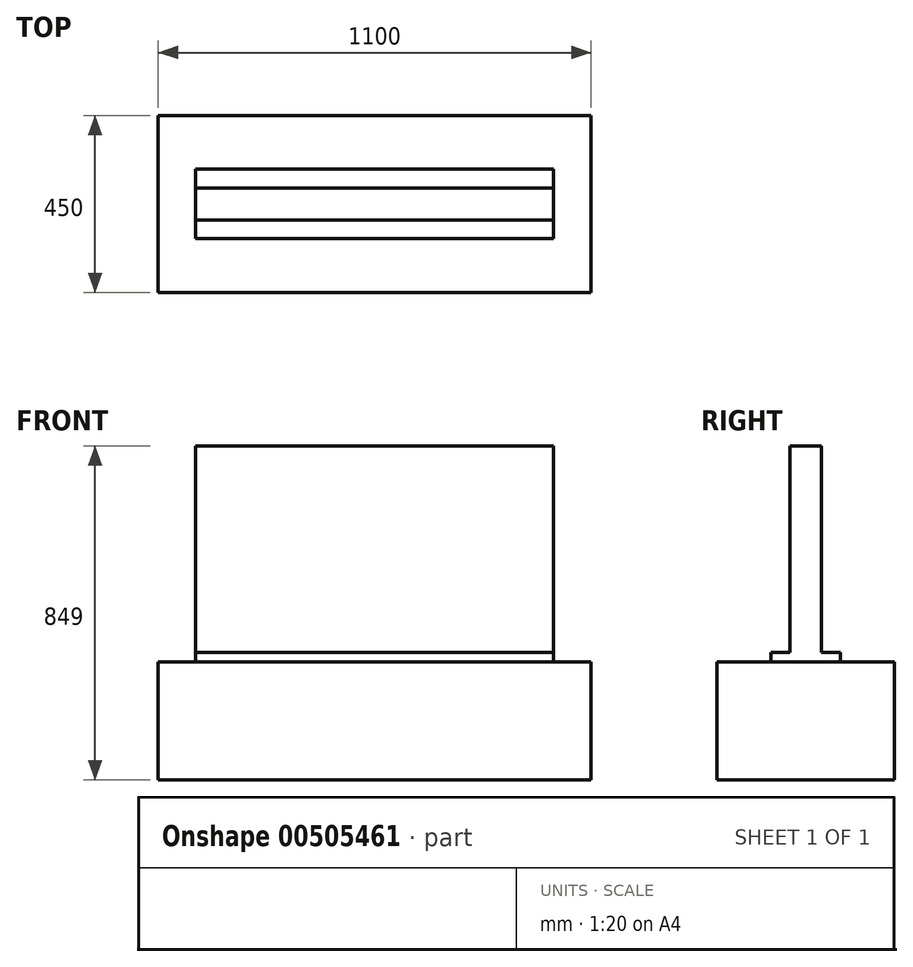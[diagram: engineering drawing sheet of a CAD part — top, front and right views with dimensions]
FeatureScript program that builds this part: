
annotation { "Feature Type Name" : "Feature", "Feature Type Description" : "" }
export const myFeature = defineFeature(function(context is Context, id is Id, definition is map)
    precondition{}
    {
        {
            var Q0;
            Q0=qCreatedBy(makeId("Top.planeOp"),FACE);
            var sketch = newSketch(context, id + "F0", { "sketchPlane" : qUnion([Q0])});
            skLineSegment(sketch, "E0.bottom", {"start": v(-454.5, 40.5) * mm, "end": v(454.5, 40.5) * mm});
            skLineSegment(sketch, "E0.top", {"start": v(-454.5, -40.5) * mm, "end": v(454.5, -40.5) * mm});
            skLineSegment(sketch, "E0.left", {"start": v(-454.5, 40.5) * mm, "end": v(-454.5, -40.5) * mm});
            skLineSegment(sketch, "E0.right", {"start": v(454.5, 40.5) * mm, "end": v(454.5, -40.5) * mm});
            skPoint(sketch, "E0.middle", {"position": v(0, 0) * mm});
            skSolve(sketch);
        }
        {
            var Q0;
            Q0 = qSketchRegion(id + "F0", true);
            extrude(context, id + "F1", {"entities" : qUnion([Q0]), "depth" : 549 * mm});
        }
        {
            var Q0;
            Q0=makeQuery(id+"F1.opExtrude","CAP_FACE",FACE,{"disambiguationData":[OSD([sQuery(id+"F0.wireOp",EDGE,"E0.bottom"),sQuery(id+"F0.wireOp",EDGE,"E0.top"),sQuery(id+"F0.wireOp",EDGE,"E0.left"),sQuery(id+"F0.wireOp",EDGE,"E0.right")])],"isStart":true});
            var sketch = newSketch(context, id + "F2", { "sketchPlane" : qUnion([Q0])});
            skLineSegment(sketch, "E1.bottom", {"start": v(454.5, -88) * mm, "end": v(-454.5, -88) * mm});
            skLineSegment(sketch, "E1.top", {"start": v(454.5, 88) * mm, "end": v(-454.5, 88) * mm});
            skLineSegment(sketch, "E1.left", {"start": v(454.5, -88) * mm, "end": v(454.5, 88) * mm});
            skLineSegment(sketch, "E1.right", {"start": v(-454.5, -88) * mm, "end": v(-454.5, 88) * mm});
            skPoint(sketch, "E1.middle", {"position": v(0, 0) * mm});
            skSolve(sketch);
        }
        {
            var Q0;
            Q0 = qSketchRegion(id + "F2", true);
            extrude(context, id + "F3", {"entities" : qUnion([Q0]), "operationType" : NewBodyOperationType.ADD, "oppositeDirection" : true, "depth" : 25 * mm});
        }
        {
            var Q0;
            Q0=makeQuery(id+"F3.boolean.opBoolean","MERGE",FACE,{"derivedFrom":[makeQuery(id+"F1.opExtrude","CAP_FACE",FACE,{"disambiguationData":[OSD([sQuery(id+"F0.wireOp",EDGE,"E0.bottom"),sQuery(id+"F0.wireOp",EDGE,"E0.top"),sQuery(id+"F0.wireOp",EDGE,"E0.left"),sQuery(id+"F0.wireOp",EDGE,"E0.right")])],"isStart":true}),makeQuery(id+"F3.opExtrude","CAP_FACE",FACE,{"disambiguationData":[OSD([sQuery(id+"F2.wireOp",EDGE,"E1.bottom"),sQuery(id+"F2.wireOp",EDGE,"E1.top"),sQuery(id+"F2.wireOp",EDGE,"E1.left"),sQuery(id+"F2.wireOp",EDGE,"E1.right")])],"isStart":true})]});
            var sketch = newSketch(context, id + "F4", { "sketchPlane" : qUnion([Q0])});
            skLineSegment(sketch, "E2.bottom", {"start": v(550, -225) * mm, "end": v(-550, -225) * mm});
            skLineSegment(sketch, "E2.top", {"start": v(550, 225) * mm, "end": v(-550, 225) * mm});
            skLineSegment(sketch, "E2.left", {"start": v(550, -225) * mm, "end": v(550, 225) * mm});
            skLineSegment(sketch, "E2.right", {"start": v(-550, -225) * mm, "end": v(-550, 225) * mm});
            skPoint(sketch, "E2.middle", {"position": v(0, 0) * mm});
            skSolve(sketch);
        }
        {
            var Q0;
            Q0 = qSketchRegion(id + "F4", true);
            extrude(context, id + "F5", {"entities" : qUnion([Q0]), "operationType" : NewBodyOperationType.ADD, "depth" : 300 * mm});
        }
    });
